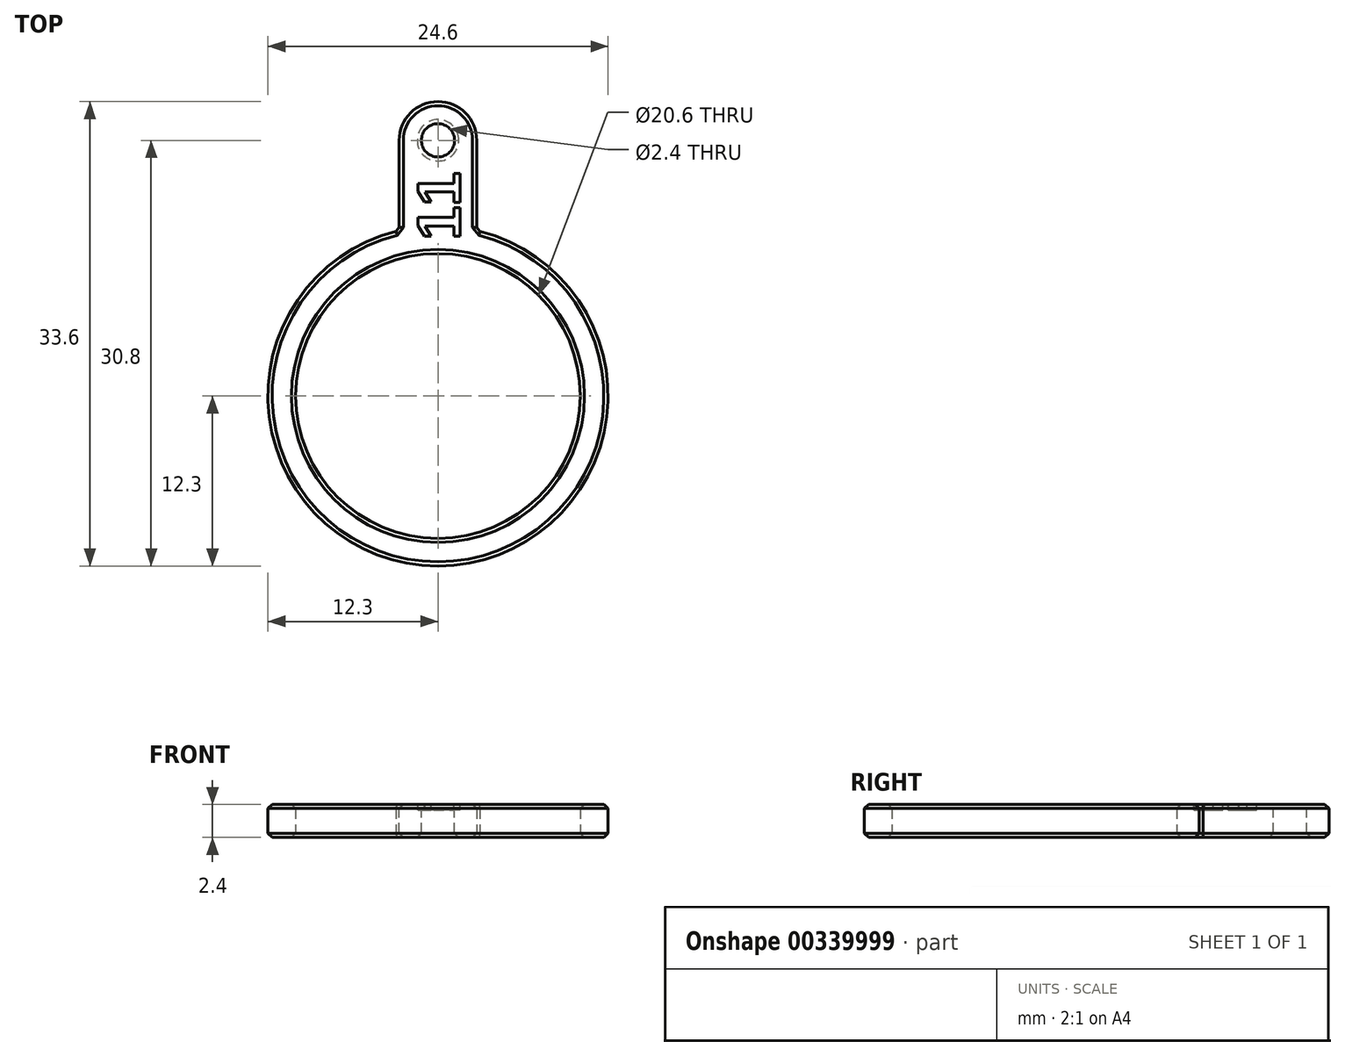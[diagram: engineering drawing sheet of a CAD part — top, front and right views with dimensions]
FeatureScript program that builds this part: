
annotation { "Feature Type Name" : "Feature", "Feature Type Description" : "" }
export const myFeature = defineFeature(function(context is Context, id is Id, definition is map)
    precondition{}
    {
        {
            var Q0;
            Q0=qCreatedBy(makeId("Top.planeOp"),FACE);
            var sketch = newSketch(context, id + "F0", { "sketchPlane" : qUnion([Q0])});
            skCircle(sketch, "E0", {"center": v(0, 0) * mm, "radius": 10.3 * mm});
            skCircle(sketch, "E1", {"center": v(0, 0) * mm, "radius": 12.3 * mm});
            skLineSegment(sketch, "E2.bottom", {"start": v(2.8, 3.3) * mm, "end": v(-2.8, 3.3) * mm});
            skLineSegment(sketch, "E2.top", {"start": v(2.8, 21.3) * mm, "end": v(-2.8, 21.3) * mm});
            skLineSegment(sketch, "E2.left", {"start": v(2.8, 3.3) * mm, "end": v(2.8, 21.3) * mm});
            skLineSegment(sketch, "E2.right", {"start": v(-2.8, 3.3) * mm, "end": v(-2.8, 21.3) * mm});
            skPoint(sketch, "E2.middle", {"position": v(0, 12.3) * mm});
            skSolve(sketch);
        }
        {
            var Q0;
            Q0=qSketchRegion(id+"F0",true);
            extrude(context, id + "F1", {"entities" : qUnion([Q0]), "depth" : 2.4 * mm});
        }
        {
            var Q0;
            Q0=makeQuery(id+"F1.opExtrude","SWEPT_EDGE",EDGE,{"disambiguationData":[OSD([sQuery(id+"F0.wireOp",EDGE,"E2.top"),sQuery(id+"F0.wireOp",EDGE,"E2.right")])]});
            var Q1;
            Q1=makeQuery(id+"F1.opExtrude","SWEPT_EDGE",EDGE,{"disambiguationData":[OSD([sQuery(id+"F0.wireOp",EDGE,"E2.top"),sQuery(id+"F0.wireOp",EDGE,"E2.left")])]});
            fillet(context, id + "F2", {"entities" : qUnion([Q0, Q1]), "radius" : 2.8 * mm, "tangentPropagation" : true, "allowEdgeOverflow" : false});
        }
        {
            var Q0;
            Q0=makeQuery(id+"F1.opExtrude","CAP_FACE",FACE,{"disambiguationData":[OSD([sQuery(id+"F0.wireOp",EDGE,"E0"),sQuery(id+"F0.wireOp",EDGE,"E1"),sQuery(id+"F0.wireOp",EDGE,"E2.top"),sQuery(id+"F0.wireOp",EDGE,"E2.left"),sQuery(id+"F0.wireOp",EDGE,"E2.right")])],"isStart":false});
            var sketch = newSketch(context, id + "F3", { "sketchPlane" : qUnion([Q0])});
            skCircle(sketch, "E3", {"center": v(0, 18.5) * mm, "radius": 1.2 * mm});
            skSolve(sketch);
        }
        {
            var Q0;
            Q0=qSketchRegion(id+"F3",true);
            extrude(context, id + "F4", {"entities" : qUnion([Q0]), "operationType" : NewBodyOperationType.REMOVE, "oppositeDirection" : true, "depth" : 25 * mm});
        }
        {
            var Q0;
            Q0=makeQuery(id+"F4.boolean.opBoolean","COPY",EDGE,{"derivedFrom":makeQuery(id+"F4.opExtrude","CAP_EDGE",EDGE,{"disambiguationData":[OSD([sQuery(id+"F3.wireOp",EDGE,"E3")])],"isStart":true})});
            var Q1;
            Q1=makeQuery(id+"F4.boolean.opBoolean","INTERSECT",EDGE,{"derivedFrom":[makeQuery(id+"F1.opExtrude","CAP_FACE",FACE,{"disambiguationData":[OSD([sQuery(id+"F0.wireOp",EDGE,"E0"),sQuery(id+"F0.wireOp",EDGE,"E1"),sQuery(id+"F0.wireOp",EDGE,"E2.top"),sQuery(id+"F0.wireOp",EDGE,"E2.left"),sQuery(id+"F0.wireOp",EDGE,"E2.right")])],"isStart":true}),makeQuery(id+"F4.opExtrude","SWEPT_FACE",FACE,{"disambiguationData":[OSD([sQuery(id+"F3.wireOp",EDGE,"E3")])]})]});
            var Q2;
            {var subQ0=sQuery(id+"F0.wireOp",EDGE,"E2.right");var subQ1=sQuery(id+"F0.wireOp",EDGE,"E2.top");Q2=makeQuery(id+"F2.opFillet","BLEND_EDGE",EDGE,{"blendedFrom":[makeQuery(id+"F1.opExtrude","SWEPT_EDGE",EDGE,{"disambiguationData":[OSD([subQ1,subQ0])]}),makeQuery(id+"F1.opExtrude","CAP_FACE",FACE,{"disambiguationData":[OSD([sQuery(id+"F0.wireOp",EDGE,"E0"),sQuery(id+"F0.wireOp",EDGE,"E1"),subQ1,sQuery(id+"F0.wireOp",EDGE,"E2.left"),subQ0])],"isStart":true})],"blendedInto":[makeQuery(id+"F1.opExtrude","CAP_FACE",FACE,{"disambiguationData":[OSD([sQuery(id+"F0.wireOp",EDGE,"E0"),sQuery(id+"F0.wireOp",EDGE,"E1"),subQ1,sQuery(id+"F0.wireOp",EDGE,"E2.left"),subQ0])],"isStart":true})]});}
            var Q3;
            {var subQ0=sQuery(id+"F0.wireOp",EDGE,"E2.right");var subQ1=sQuery(id+"F0.wireOp",EDGE,"E2.top");Q3=makeQuery(id+"F2.opFillet","BLEND_EDGE",EDGE,{"blendedFrom":[makeQuery(id+"F1.opExtrude","SWEPT_EDGE",EDGE,{"disambiguationData":[OSD([subQ1,subQ0])]}),makeQuery(id+"F1.opExtrude","CAP_FACE",FACE,{"disambiguationData":[OSD([sQuery(id+"F0.wireOp",EDGE,"E0"),sQuery(id+"F0.wireOp",EDGE,"E1"),subQ1,sQuery(id+"F0.wireOp",EDGE,"E2.left"),subQ0])],"isStart":false})],"blendedInto":[makeQuery(id+"F1.opExtrude","CAP_FACE",FACE,{"disambiguationData":[OSD([sQuery(id+"F0.wireOp",EDGE,"E0"),sQuery(id+"F0.wireOp",EDGE,"E1"),subQ1,sQuery(id+"F0.wireOp",EDGE,"E2.left"),subQ0])],"isStart":false})]});}
            var Q4;
            Q4=makeQuery(id+"F1.opExtrude","CAP_EDGE",EDGE,{"disambiguationData":[OSD([sQuery(id+"F0.wireOp",EDGE,"E1")])],"isStart":false});
            var Q5;
            Q5=makeQuery(id+"F1.opExtrude","CAP_EDGE",EDGE,{"disambiguationData":[OSD([sQuery(id+"F0.wireOp",EDGE,"E1")])],"isStart":true});
            var Q6;
            Q6=makeQuery(id+"F1.opExtrude","SWEPT_EDGE",EDGE,{"disambiguationData":[OSD([sQuery(id+"F0.wireOp",EDGE,"E1"),sQuery(id+"F0.wireOp",EDGE,"E2.left")])]});
            var Q7;
            Q7=makeQuery(id+"F1.opExtrude","SWEPT_EDGE",EDGE,{"disambiguationData":[OSD([sQuery(id+"F0.wireOp",EDGE,"E1"),sQuery(id+"F0.wireOp",EDGE,"E2.right")])]});
            var Q8;
            Q8=makeQuery(id+"F1.opExtrude","CAP_EDGE",EDGE,{"disambiguationData":[OSD([sQuery(id+"F0.wireOp",EDGE,"E0")])],"isStart":true});
            var Q9;
            Q9=makeQuery(id+"F1.opExtrude","CAP_EDGE",EDGE,{"disambiguationData":[OSD([sQuery(id+"F0.wireOp",EDGE,"E0")])],"isStart":false});
            chamfer(context, id + "F5", {"entities" : qUnion([Q0, Q1, Q2, Q3, Q4, Q5, Q6, Q7, Q8, Q9]), "width" : 0.3 * mm, "tangentPropagation" : true});
        }
        {
            var Q0;
            Q0=makeQuery(id+"F1.opExtrude","CAP_FACE",FACE,{"disambiguationData":[OSD([sQuery(id+"F0.wireOp",EDGE,"E0"),sQuery(id+"F0.wireOp",EDGE,"E1"),sQuery(id+"F0.wireOp",EDGE,"E2.top"),sQuery(id+"F0.wireOp",EDGE,"E2.left"),sQuery(id+"F0.wireOp",EDGE,"E2.right")])],"isStart":false});
            var sketch = newSketch(context, id + "F6", { "sketchPlane" : qUnion([Q0])});
            skText(sketch, "E4", { "text": "11\n", "fontName": "Arimo-Bold.ttf"});
            skLineSegment(sketch, "E5", {"start": v(0, 11.27) * mm, "end": v(0, 0) * mm});
            skPoint(sketch, "E5.endSnap0", {"position": v(0, 11.27) * mm});
            const initialGuessF6  = {"E4": [0.0016, 0.01127, 0, 1, 0.0032]};
            skSetInitialGuess(sketch, initialGuessF6);
            skSolve(sketch);
        }
        {
            var Q0;
            Q0=qSketchRegion(id+"F6",true);
            extrude(context, id + "F7", {"entities" : qUnion([Q0]), "operationType" : NewBodyOperationType.REMOVE, "oppositeDirection" : true, "depth" : 0.4 * mm});
        }
    });
